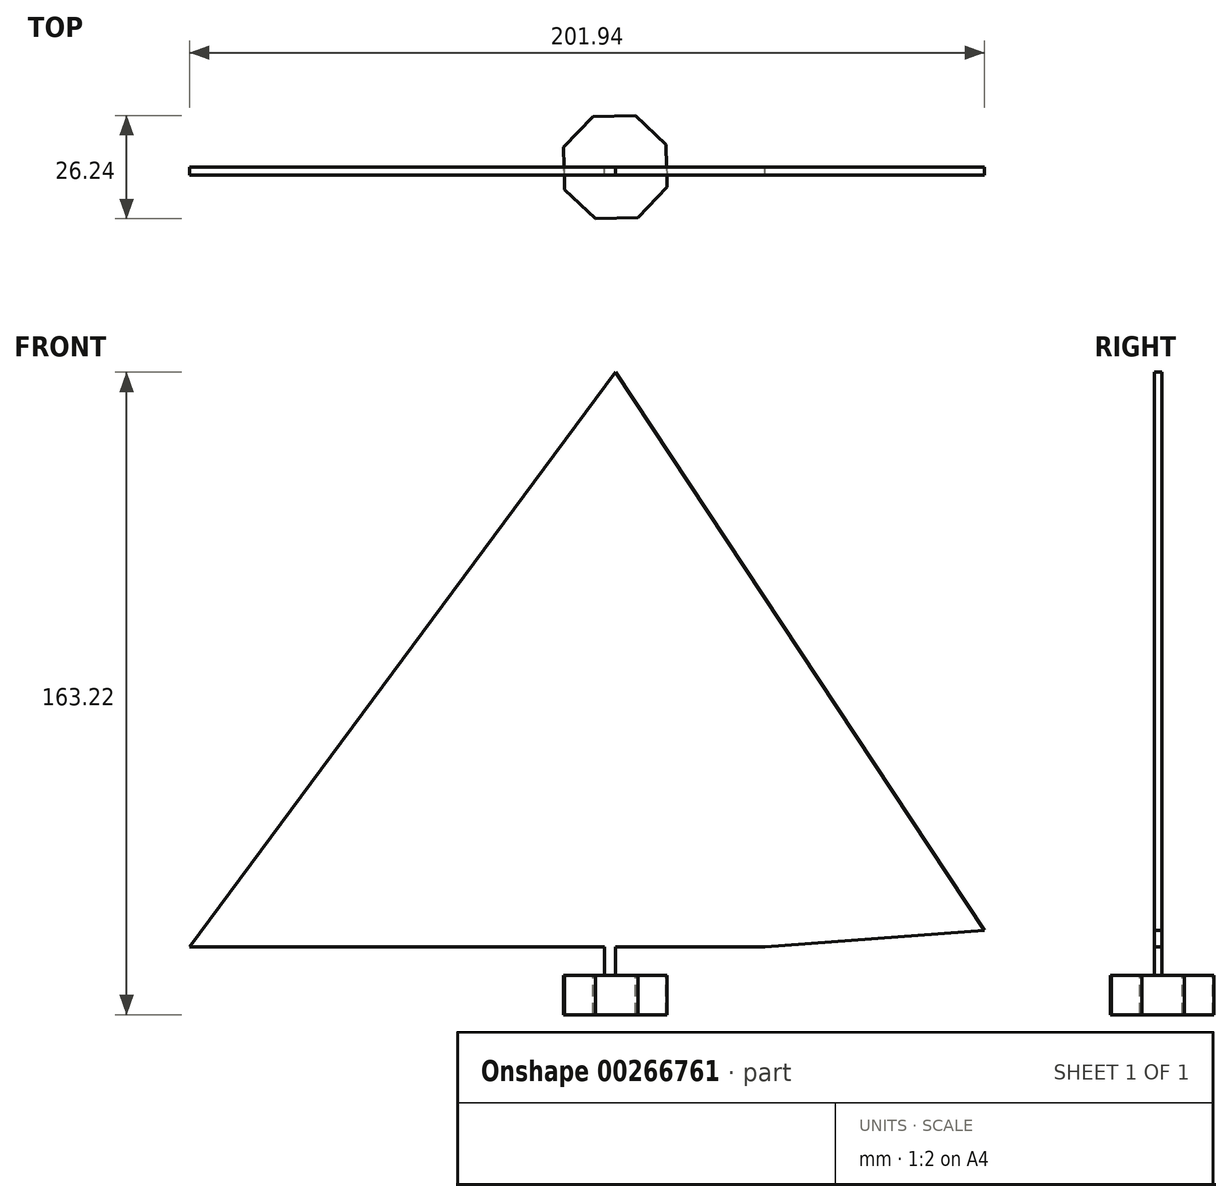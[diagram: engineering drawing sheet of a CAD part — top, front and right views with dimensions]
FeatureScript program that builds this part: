
annotation { "Feature Type Name" : "Feature", "Feature Type Description" : "" }
export const myFeature = defineFeature(function(context is Context, id is Id, definition is map)
    precondition{}
    {
        {
            var Q0;
            Q0=qCreatedBy(makeId("Top.planeOp"),FACE);
            var sketch = newSketch(context, id + "F0", { "sketchPlane" : qUnion([Q0])});
            skCircle(sketch, "E0.cCircle", {"center": v(0, 0) * mm, "radius": 13 * mm, "construction": true});
            skLineSegment(sketch, "E0.0", {"start": v(-13.12, 5.09) * mm, "end": v(-5.68, 12.88) * mm});
            skLineSegment(sketch, "E0.1", {"start": v(-5.68, 12.88) * mm, "end": v(5.09, 13.12) * mm});
            skLineSegment(sketch, "E0.2", {"start": v(5.09, 13.12) * mm, "end": v(12.88, 5.68) * mm});
            skLineSegment(sketch, "E0.3", {"start": v(12.88, 5.68) * mm, "end": v(13.12, -5.09) * mm});
            skLineSegment(sketch, "E0.4", {"start": v(13.12, -5.09) * mm, "end": v(5.68, -12.88) * mm});
            skLineSegment(sketch, "E0.5", {"start": v(5.68, -12.88) * mm, "end": v(-5.09, -13.12) * mm});
            skLineSegment(sketch, "E0.6", {"start": v(-5.09, -13.12) * mm, "end": v(-12.88, -5.68) * mm});
            skLineSegment(sketch, "E0.7", {"start": v(-12.88, -5.68) * mm, "end": v(-13.12, 5.09) * mm});
            skPoint(sketch, "E0.0.midPoint", {"position": v(-9.4, 8.98) * mm});
            skSolve(sketch);
        }
        {
            var Q0;
            Q0=makeQuery(id+"F0.imprint","IMPRINT",FACE,{"disambiguationData":[TD([[makeQuery(id+"F0.imprint","IMPRINT",EDGE,{"derivedFrom":sQuery(id+"F0.wireOp",EDGE,"E0.0")}),-1.0]])]});
            extrude(context, id + "F1", {"entities" : qUnion([Q0]), "oppositeDirection" : true, "depth" : 10 * mm});
        }
        {
            var Q0;
            Q0=qCreatedBy(makeId("Front.planeOp"),FACE);
            var sketch = newSketch(context, id + "F2", { "sketchPlane" : qUnion([Q0])});
            skLineSegment(sketch, "E1", {"start": v(0, 0) * mm, "end": v(0, 14.56) * mm});
            skLineSegment(sketch, "E2", {"start": v(-31.36, 14.56) * mm, "end": v(0, 55.32) * mm});
            skLineSegment(sketch, "E3", {"start": v(0, 55.32) * mm, "end": v(0, 42.57) * mm});
            skLineSegment(sketch, "E4", {"start": v(-31.36, 14.56) * mm, "end": v(-5.62, 14.56) * mm});
            skLineSegment(sketch, "E5", {"start": v(-5.62, 14.56) * mm, "end": v(-2.8, 7.28) * mm});
            skLineSegment(sketch, "E6", {"start": v(0, 42.57) * mm, "end": v(0, 55.32) * mm});
            skLineSegment(sketch, "E7", {"start": v(0, 0) * mm, "end": v(-2.8, 0) * mm});
            skLineSegment(sketch, "E8", {"start": v(-2.8, 0) * mm, "end": v(-2.8, 7.28) * mm});
            skPoint(sketch, "E8.endSnap0", {"position": v(-2.8, 7.28) * mm});
            skLineSegment(sketch, "E9", {"start": v(-2.8, 7.28) * mm, "end": v(-2.8, 7.28) * mm});
            skLineSegment(sketch, "E10", {"start": v(0, 14.56) * mm, "end": v(20.74, 14.56) * mm});
            skLineSegment(sketch, "E11", {"start": v(20.74, 14.56) * mm, "end": v(0, 42.57) * mm});
            skLineSegment(sketch, "E12", {"start": v(-2.8, 7.28) * mm, "end": v(-49.32, 7.28) * mm});
            skLineSegment(sketch, "E13", {"start": v(-49.32, 7.28) * mm, "end": v(0, 90.1) * mm});
            skLineSegment(sketch, "E14", {"start": v(0, 90.1) * mm, "end": v(0, 62.5) * mm});
            skLineSegment(sketch, "E15", {"start": v(0, 62.5) * mm, "end": v(38.02, 7.28) * mm});
            skLineSegment(sketch, "E16", {"start": v(38.02, 7.28) * mm, "end": v(0, 7.28) * mm});
            skLineSegment(sketch, "E17", {"start": v(-49.32, 7.28) * mm, "end": v(-108.16, 7.28) * mm});
            skLineSegment(sketch, "E18", {"start": v(-108.16, 7.28) * mm, "end": v(0, 153.22) * mm});
            skLineSegment(sketch, "E19", {"start": v(0, 153.22) * mm, "end": v(93.78, 11.4) * mm});
            skLineSegment(sketch, "E20", {"start": v(93.78, 11.4) * mm, "end": v(38.02, 7.28) * mm});
            skSolve(sketch);
        }
        {
            var Q0;
            Q0=makeQuery(id+"F2.imprint","IMPRINT",FACE,{"disambiguationData":[TD([[makeQuery(id+"F2.imprint","IMPRINT",EDGE,{"derivedFrom":sQuery(id+"F2.wireOp",EDGE,"E1")}),1.0]])]});
            var Q1;
            Q1=makeQuery(id+"F2.imprint","IMPRINT",FACE,{"disambiguationData":[TD([[makeQuery(id+"F2.imprint","IMPRINT",EDGE,{"derivedFrom":sQuery(id+"F2.wireOp",EDGE,"E2")}),1.0]])]});
            var Q2;
            Q2=makeQuery(id+"F2.imprint","IMPRINT",FACE,{"disambiguationData":[TD([[makeQuery(id+"F2.imprint","IMPRINT",EDGE,{"derivedFrom":sQuery(id+"F2.wireOp",EDGE,"E13")}),1.0]])]});
            extrude(context, id + "F3", {"entities" : qUnion([Q0, Q1, Q2]), "depth" : 2 * mm});
        }
    });
